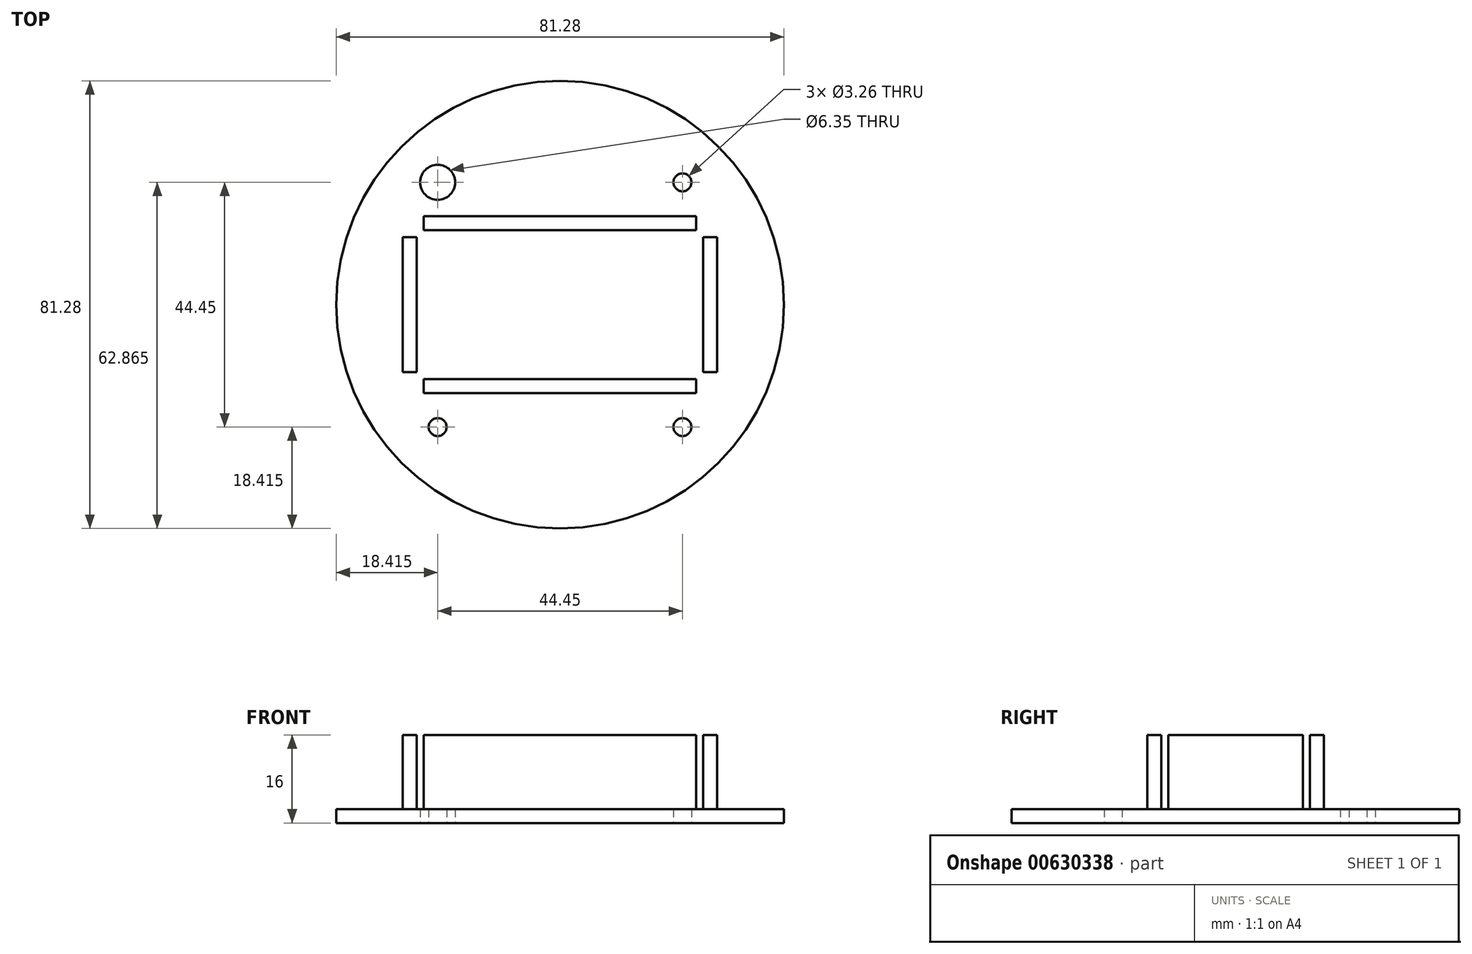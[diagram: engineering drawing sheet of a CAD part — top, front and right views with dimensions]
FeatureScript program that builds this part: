
annotation { "Feature Type Name" : "Feature", "Feature Type Description" : "" }
export const myFeature = defineFeature(function(context is Context, id is Id, definition is map)
    precondition{}
    {
        {
            var Q0;
            Q0=qCreatedBy(makeId("Top.planeOp"),FACE);
            var sketch = newSketch(context, id + "F0", { "sketchPlane" : qUnion([Q0])});
            skLineSegment(sketch, "E0.bottom", {"start": v(-25.4, 25.4) * mm, "end": v(25.4, 25.4) * mm});
            skLineSegment(sketch, "E0.top", {"start": v(-25.4, -25.4) * mm, "end": v(25.4, -25.4) * mm});
            skLineSegment(sketch, "E0.left", {"start": v(-25.4, 25.4) * mm, "end": v(-25.4, -25.4) * mm});
            skLineSegment(sketch, "E0.right", {"start": v(25.4, 25.4) * mm, "end": v(25.4, -25.4) * mm});
            skPoint(sketch, "E0.middle", {"position": v(0, 0) * mm});
            skCircle(sketch, "E1", {"center": v(-22.23, -22.23) * mm, "radius": 1.63 * mm});
            skCircle(sketch, "E2", {"center": v(22.22, 22.23) * mm, "radius": 1.63 * mm});
            skCircle(sketch, "E3", {"center": v(0, 0) * mm, "radius": 38.1 * mm});
            skCircle(sketch, "E4", {"center": v(0, 0) * mm, "radius": 40.64 * mm});
            skLineSegment(sketch, "E5", {"start": v(-25.4, -25.4) * mm, "end": v(25.4, 25.4) * mm});
            skLineSegment(sketch, "E6", {"start": v(-25.4, 25.4) * mm, "end": v(25.4, -25.4) * mm});
            skCircle(sketch, "E7", {"center": v(-22.23, -22.23) * mm, "radius": 3.18 * mm});
            skLineSegment(sketch, "E8", {"start": v(-22.6, -18.12) * mm, "end": v(-33.07, -28.58) * mm});
            skLineSegment(sketch, "E9", {"start": v(-17.1, -21.6) * mm, "end": v(-27.95, -32.44) * mm});
            skCircle(sketch, "E10", {"center": v(22.22, 22.23) * mm, "radius": 3.18 * mm});
            skLineSegment(sketch, "E11", {"start": v(27.08, 31.57) * mm, "end": v(15.84, 20.33) * mm});
            skLineSegment(sketch, "E12", {"start": v(21.85, 17.36) * mm, "end": v(33.43, 28.94) * mm});
            skCircle(sketch, "E13", {"center": v(-22.23, 22.23) * mm, "radius": 1.63 * mm});
            skCircle(sketch, "E14", {"center": v(22.23, -22.23) * mm, "radius": 1.63 * mm});
            skCircle(sketch, "E15", {"center": v(-22.23, 22.23) * mm, "radius": 3.18 * mm});
            skLineSegment(sketch, "E16", {"start": v(-24.44, 19.95) * mm, "end": v(-31.62, 27.13) * mm});
            skLineSegment(sketch, "E17", {"start": v(-19.9, 24.4) * mm, "end": v(-27.14, 31.63) * mm});
            skCircle(sketch, "E18", {"center": v(22.23, -22.23) * mm, "radius": 3.18 * mm});
            skLineSegment(sketch, "E19", {"start": v(19.8, -24.28) * mm, "end": v(28.43, -32.92) * mm});
            skLineSegment(sketch, "E20", {"start": v(23.82, -19.33) * mm, "end": v(35.07, -30.58) * mm});
            skSolve(sketch);
        }
        {
            var Q0;
            {var subQ0=sQuery(id+"F0.wireOp",EDGE,"E16");var subQ1=sQuery(id+"F0.wireOp",EDGE,"E3");var subQ2=makeQuery(id+"F0.imprint","INTERSECT",VERTEX,{"derivedFrom":[subQ1,subQ0]});Q0=makeQuery(id+"F0.imprint","IMPRINT",FACE,{"disambiguationData":[TD([[makeQuery(id+"F0.imprint","IMPRINT",EDGE,{"disambiguationData":[TD([[subQ2,-1.0]])],"derivedFrom":subQ1}),-1.0]])]});}
            var Q1;
            {var subQ0=sQuery(id+"F0.wireOp",EDGE,"E17");var subQ1=sQuery(id+"F0.wireOp",EDGE,"E3");var subQ2=makeQuery(id+"F0.imprint","INTERSECT",VERTEX,{"derivedFrom":[subQ1,subQ0]});Q1=makeQuery(id+"F0.imprint","IMPRINT",FACE,{"disambiguationData":[TD([[makeQuery(id+"F0.imprint","IMPRINT",EDGE,{"disambiguationData":[TD([[subQ2,-1.0]])],"derivedFrom":subQ1}),-1.0]])]});}
            var Q2;
            {var subQ0=sQuery(id+"F0.wireOp",EDGE,"E11");var subQ1=sQuery(id+"F0.wireOp",EDGE,"E3");var subQ2=makeQuery(id+"F0.imprint","INTERSECT",VERTEX,{"derivedFrom":[subQ1,subQ0]});Q2=makeQuery(id+"F0.imprint","IMPRINT",FACE,{"disambiguationData":[TD([[makeQuery(id+"F0.imprint","IMPRINT",EDGE,{"disambiguationData":[TD([[subQ2,-1.0]])],"derivedFrom":subQ1}),-1.0]])]});}
            var Q3;
            {var subQ0=sQuery(id+"F0.wireOp",EDGE,"E11");var subQ1=sQuery(id+"F0.wireOp",EDGE,"E3");var subQ2=makeQuery(id+"F0.imprint","INTERSECT",VERTEX,{"derivedFrom":[subQ1,subQ0]});Q3=makeQuery(id+"F0.imprint","IMPRINT",FACE,{"disambiguationData":[TD([[makeQuery(id+"F0.imprint","IMPRINT",EDGE,{"disambiguationData":[TD([[subQ2,1.0]])],"derivedFrom":subQ1}),-1.0]])]});}
            var Q4;
            {var subQ0=sQuery(id+"F0.wireOp",EDGE,"E12");var subQ1=sQuery(id+"F0.wireOp",EDGE,"E3");var subQ2=makeQuery(id+"F0.imprint","INTERSECT",VERTEX,{"derivedFrom":[subQ1,subQ0]});Q4=makeQuery(id+"F0.imprint","IMPRINT",FACE,{"disambiguationData":[TD([[makeQuery(id+"F0.imprint","IMPRINT",EDGE,{"disambiguationData":[TD([[subQ2,1.0]])],"derivedFrom":subQ1}),-1.0]])]});}
            var Q5;
            {var subQ0=sQuery(id+"F0.wireOp",EDGE,"E19");var subQ1=sQuery(id+"F0.wireOp",EDGE,"E3");var subQ2=makeQuery(id+"F0.imprint","INTERSECT",VERTEX,{"derivedFrom":[subQ1,subQ0]});Q5=makeQuery(id+"F0.imprint","IMPRINT",FACE,{"disambiguationData":[TD([[makeQuery(id+"F0.imprint","IMPRINT",EDGE,{"disambiguationData":[TD([[subQ2,-1.0]])],"derivedFrom":subQ1}),-1.0]])]});}
            var Q6;
            {var subQ0=sQuery(id+"F0.wireOp",EDGE,"E8");var subQ1=sQuery(id+"F0.wireOp",EDGE,"E3");var subQ2=makeQuery(id+"F0.imprint","INTERSECT",VERTEX,{"derivedFrom":[subQ1,subQ0]});Q6=makeQuery(id+"F0.imprint","IMPRINT",FACE,{"disambiguationData":[TD([[makeQuery(id+"F0.imprint","IMPRINT",EDGE,{"disambiguationData":[TD([[subQ2,-1.0]])],"derivedFrom":subQ1}),-1.0]])]});}
            var Q7;
            {var subQ0=sQuery(id+"F0.wireOp",EDGE,"E16");var subQ1=sQuery(id+"F0.wireOp",EDGE,"E0.left");var subQ2=makeQuery(id+"F0.imprint","INTERSECT",VERTEX,{"derivedFrom":[subQ1,subQ0]});Q7=makeQuery(id+"F0.imprint","IMPRINT",FACE,{"disambiguationData":[TD([[makeQuery(id+"F0.imprint","IMPRINT",EDGE,{"disambiguationData":[TD([[subQ2,-1.0]])],"derivedFrom":subQ1}),-1.0]])]});}
            var Q8;
            {var subQ7=sQuery(id+"F0.wireOp",EDGE,"E0.bottom");var subQ10=sQuery(id+"F0.wireOp",EDGE,"E11");var subQ11=makeQuery(id+"F0.imprint","INTERSECT",VERTEX,{"derivedFrom":[subQ7,subQ10]});Q8=makeQuery(id+"F0.imprint","IMPRINT",FACE,{"disambiguationData":[TD([[makeQuery(id+"F0.imprint","IMPRINT",EDGE,{"disambiguationData":[TD([[subQ11,-1.0]])],"derivedFrom":subQ7}),1.0]])]});}
            var Q9;
            {var subQ1=sQuery(id+"F0.wireOp",EDGE,"E0.top");var subQ5=sQuery(id+"F0.wireOp",EDGE,"E19");var subQ6=makeQuery(id+"F0.imprint","INTERSECT",VERTEX,{"derivedFrom":[subQ1,subQ5]});Q9=makeQuery(id+"F0.imprint","IMPRINT",FACE,{"disambiguationData":[TD([[makeQuery(id+"F0.imprint","IMPRINT",EDGE,{"disambiguationData":[TD([[subQ6,-1.0]])],"derivedFrom":subQ1}),-1.0]])]});}
            var Q10;
            {var subQ1=sQuery(id+"F0.wireOp",EDGE,"E0.top");var subQ3=sQuery(id+"F0.wireOp",EDGE,"E7");var subQ7=makeQuery(id+"F0.imprint","INTERSECT",VERTEX,{"derivedFrom":[subQ1,subQ3]});Q10=makeQuery(id+"F0.imprint","IMPRINT",FACE,{"disambiguationData":[TD([[makeQuery(id+"F0.imprint","IMPRINT",EDGE,{"disambiguationData":[TD([[subQ7,-1.0]])],"derivedFrom":subQ1}),-1.0]])]});}
            var Q11;
            {var subQ0=sQuery(id+"F0.wireOp",EDGE,"E9");var subQ1=sQuery(id+"F0.wireOp",EDGE,"E0.top");var subQ2=makeQuery(id+"F0.imprint","INTERSECT",VERTEX,{"derivedFrom":[subQ1,subQ0]});Q11=makeQuery(id+"F0.imprint","IMPRINT",FACE,{"disambiguationData":[TD([[makeQuery(id+"F0.imprint","IMPRINT",EDGE,{"disambiguationData":[TD([[subQ2,-1.0]])],"derivedFrom":subQ1}),-1.0]])]});}
            var Q12;
            {var subQ0=sQuery(id+"F0.wireOp",EDGE,"E9");var subQ1=sQuery(id+"F0.wireOp",EDGE,"E3");var subQ2=makeQuery(id+"F0.imprint","INTERSECT",VERTEX,{"derivedFrom":[subQ1,subQ0]});Q12=makeQuery(id+"F0.imprint","IMPRINT",FACE,{"disambiguationData":[TD([[makeQuery(id+"F0.imprint","IMPRINT",EDGE,{"disambiguationData":[TD([[subQ2,-1.0]])],"derivedFrom":subQ1}),-1.0]])]});}
            var Q13;
            {var subQ1=sQuery(id+"F0.wireOp",EDGE,"E0.left");var subQ3=sQuery(id+"F0.wireOp",EDGE,"E7");var subQ4=makeQuery(id+"F0.imprint","INTERSECT",VERTEX,{"derivedFrom":[subQ1,subQ3]});Q13=makeQuery(id+"F0.imprint","IMPRINT",FACE,{"disambiguationData":[TD([[makeQuery(id+"F0.imprint","IMPRINT",EDGE,{"disambiguationData":[TD([[subQ4,-1.0]])],"derivedFrom":subQ3}),-1.0]])]});}
            var Q14;
            {var subQ1=sQuery(id+"F0.wireOp",EDGE,"E0.top");var subQ3=sQuery(id+"F0.wireOp",EDGE,"E7");var subQ4=makeQuery(id+"F0.imprint","INTERSECT",VERTEX,{"derivedFrom":[subQ1,subQ3]});Q14=makeQuery(id+"F0.imprint","IMPRINT",FACE,{"disambiguationData":[TD([[makeQuery(id+"F0.imprint","IMPRINT",EDGE,{"disambiguationData":[TD([[subQ4,1.0]])],"derivedFrom":subQ3}),-1.0]])]});}
            var Q15;
            {var subQ0=sQuery(id+"F0.wireOp",EDGE,"E5");var subQ1=sQuery(id+"F0.wireOp",EDGE,"E1");var subQ5=makeQuery(id+"F0.imprint","INTERSECT",VERTEX,{"disambiguationData":[OD(0.0)],"derivedFrom":[subQ1,subQ0]});Q15=makeQuery(id+"F0.imprint","IMPRINT",FACE,{"disambiguationData":[TD([[makeQuery(id+"F0.imprint","IMPRINT",EDGE,{"disambiguationData":[TD([[subQ5,1.0]])],"derivedFrom":subQ1}),-1.0]])]});}
            var Q16;
            {var subQ2=sQuery(id+"F0.wireOp",EDGE,"E5");var subQ4=sQuery(id+"F0.wireOp",EDGE,"E1");var subQ5=makeQuery(id+"F0.imprint","INTERSECT",VERTEX,{"disambiguationData":[OD(0.0)],"derivedFrom":[subQ4,subQ2]});Q16=makeQuery(id+"F0.imprint","IMPRINT",FACE,{"disambiguationData":[TD([[makeQuery(id+"F0.imprint","IMPRINT",EDGE,{"disambiguationData":[TD([[subQ5,-1.0]])],"derivedFrom":subQ4}),-1.0]])]});}
            var Q17;
            {var subQ0=sQuery(id+"F0.wireOp",EDGE,"E8");var subQ1=sQuery(id+"F0.wireOp",EDGE,"E0.left");var subQ2=makeQuery(id+"F0.imprint","INTERSECT",VERTEX,{"derivedFrom":[subQ1,subQ0]});Q17=makeQuery(id+"F0.imprint","IMPRINT",FACE,{"disambiguationData":[TD([[makeQuery(id+"F0.imprint","IMPRINT",EDGE,{"disambiguationData":[TD([[subQ2,-1.0]])],"derivedFrom":subQ1}),1.0]])]});}
            var Q18;
            {var subQ0=sQuery(id+"F0.wireOp",EDGE,"E7");var subQ1=sQuery(id+"F0.wireOp",EDGE,"E0.top");var subQ2=makeQuery(id+"F0.imprint","INTERSECT",VERTEX,{"derivedFrom":[subQ1,subQ0]});Q18=makeQuery(id+"F0.imprint","IMPRINT",FACE,{"disambiguationData":[TD([[makeQuery(id+"F0.imprint","IMPRINT",EDGE,{"disambiguationData":[TD([[subQ2,-1.0]])],"derivedFrom":subQ1}),1.0]])]});}
            var Q19;
            {var subQ9=sQuery(id+"F0.wireOp",EDGE,"E0.left");var subQ11=sQuery(id+"F0.wireOp",EDGE,"E16");var subQ12=makeQuery(id+"F0.imprint","INTERSECT",VERTEX,{"derivedFrom":[subQ9,subQ11]});Q19=makeQuery(id+"F0.imprint","IMPRINT",FACE,{"disambiguationData":[TD([[makeQuery(id+"F0.imprint","IMPRINT",EDGE,{"disambiguationData":[TD([[subQ12,-1.0]])],"derivedFrom":subQ9}),1.0]])]});}
            var Q20;
            {var subQ1=sQuery(id+"F0.wireOp",EDGE,"E0.left");var subQ3=sQuery(id+"F0.wireOp",EDGE,"E15");var subQ4=makeQuery(id+"F0.imprint","INTERSECT",VERTEX,{"derivedFrom":[subQ1,subQ3]});Q20=makeQuery(id+"F0.imprint","IMPRINT",FACE,{"disambiguationData":[TD([[makeQuery(id+"F0.imprint","IMPRINT",EDGE,{"disambiguationData":[TD([[subQ4,1.0]])],"derivedFrom":subQ3}),-1.0]])]});}
            var Q21;
            {var subQ0=sQuery(id+"F0.wireOp",EDGE,"E15");var subQ1=sQuery(id+"F0.wireOp",EDGE,"E0.left");var subQ2=makeQuery(id+"F0.imprint","INTERSECT",VERTEX,{"derivedFrom":[subQ1,subQ0]});Q21=makeQuery(id+"F0.imprint","IMPRINT",FACE,{"disambiguationData":[TD([[makeQuery(id+"F0.imprint","IMPRINT",EDGE,{"disambiguationData":[TD([[subQ2,-1.0]])],"derivedFrom":subQ1}),1.0]])]});}
            var Q22;
            {var subQ0=sQuery(id+"F0.wireOp",EDGE,"E15");var subQ1=sQuery(id+"F0.wireOp",EDGE,"E0.bottom");var subQ2=makeQuery(id+"F0.imprint","INTERSECT",VERTEX,{"derivedFrom":[subQ1,subQ0]});Q22=makeQuery(id+"F0.imprint","IMPRINT",FACE,{"disambiguationData":[TD([[makeQuery(id+"F0.imprint","IMPRINT",EDGE,{"disambiguationData":[TD([[subQ2,-1.0]])],"derivedFrom":subQ1}),-1.0]])]});}
            var Q23;
            {var subQ1=sQuery(id+"F0.wireOp",EDGE,"E0.bottom");var subQ3=sQuery(id+"F0.wireOp",EDGE,"E15");var subQ4=makeQuery(id+"F0.imprint","INTERSECT",VERTEX,{"derivedFrom":[subQ1,subQ3]});Q23=makeQuery(id+"F0.imprint","IMPRINT",FACE,{"disambiguationData":[TD([[makeQuery(id+"F0.imprint","IMPRINT",EDGE,{"disambiguationData":[TD([[subQ4,-1.0]])],"derivedFrom":subQ3}),-1.0]])]});}
            var Q24;
            {var subQ0=sQuery(id+"F0.wireOp",EDGE,"E15");var subQ5=sQuery(id+"F0.wireOp",EDGE,"E0.bottom");var subQ7=makeQuery(id+"F0.imprint","INTERSECT",VERTEX,{"derivedFrom":[subQ5,subQ0]});Q24=makeQuery(id+"F0.imprint","IMPRINT",FACE,{"disambiguationData":[TD([[makeQuery(id+"F0.imprint","IMPRINT",EDGE,{"disambiguationData":[TD([[subQ7,-1.0]])],"derivedFrom":subQ5}),1.0]])]});}
            var Q25;
            {var subQ0=sQuery(id+"F0.wireOp",EDGE,"E17");var subQ1=sQuery(id+"F0.wireOp",EDGE,"E0.bottom");var subQ2=makeQuery(id+"F0.imprint","INTERSECT",VERTEX,{"derivedFrom":[subQ1,subQ0]});Q25=makeQuery(id+"F0.imprint","IMPRINT",FACE,{"disambiguationData":[TD([[makeQuery(id+"F0.imprint","IMPRINT",EDGE,{"disambiguationData":[TD([[subQ2,-1.0]])],"derivedFrom":subQ1}),1.0]])]});}
            var Q26;
            {var subQ1=sQuery(id+"F0.wireOp",EDGE,"E0.bottom");var subQ3=sQuery(id+"F0.wireOp",EDGE,"E10");var subQ4=makeQuery(id+"F0.imprint","INTERSECT",VERTEX,{"derivedFrom":[subQ1,subQ3]});Q26=makeQuery(id+"F0.imprint","IMPRINT",FACE,{"disambiguationData":[TD([[makeQuery(id+"F0.imprint","IMPRINT",EDGE,{"disambiguationData":[TD([[subQ4,1.0]])],"derivedFrom":subQ3}),-1.0]])]});}
            var Q27;
            {var subQ1=sQuery(id+"F0.wireOp",EDGE,"E0.right");var subQ3=sQuery(id+"F0.wireOp",EDGE,"E10");var subQ4=makeQuery(id+"F0.imprint","INTERSECT",VERTEX,{"derivedFrom":[subQ1,subQ3]});Q27=makeQuery(id+"F0.imprint","IMPRINT",FACE,{"disambiguationData":[TD([[makeQuery(id+"F0.imprint","IMPRINT",EDGE,{"disambiguationData":[TD([[subQ4,-1.0]])],"derivedFrom":subQ3}),-1.0]])]});}
            var Q28;
            {var subQ0=sQuery(id+"F0.wireOp",EDGE,"E11");var subQ1=sQuery(id+"F0.wireOp",EDGE,"E0.bottom");var subQ2=makeQuery(id+"F0.imprint","INTERSECT",VERTEX,{"derivedFrom":[subQ1,subQ0]});Q28=makeQuery(id+"F0.imprint","IMPRINT",FACE,{"disambiguationData":[TD([[makeQuery(id+"F0.imprint","IMPRINT",EDGE,{"disambiguationData":[TD([[subQ2,-1.0]])],"derivedFrom":subQ1}),-1.0]])]});}
            var Q29;
            {var subQ0=sQuery(id+"F0.wireOp",EDGE,"E10");var subQ1=sQuery(id+"F0.wireOp",EDGE,"E0.right");var subQ2=makeQuery(id+"F0.imprint","INTERSECT",VERTEX,{"derivedFrom":[subQ1,subQ0]});Q29=makeQuery(id+"F0.imprint","IMPRINT",FACE,{"disambiguationData":[TD([[makeQuery(id+"F0.imprint","IMPRINT",EDGE,{"disambiguationData":[TD([[subQ2,-1.0]])],"derivedFrom":subQ1}),-1.0]])]});}
            var Q30;
            {var subQ0=sQuery(id+"F0.wireOp",EDGE,"E12");var subQ1=sQuery(id+"F0.wireOp",EDGE,"E0.right");var subQ2=makeQuery(id+"F0.imprint","INTERSECT",VERTEX,{"derivedFrom":[subQ1,subQ0]});Q30=makeQuery(id+"F0.imprint","IMPRINT",FACE,{"disambiguationData":[TD([[makeQuery(id+"F0.imprint","IMPRINT",EDGE,{"disambiguationData":[TD([[subQ2,-1.0]])],"derivedFrom":subQ1}),1.0]])]});}
            var Q31;
            {var subQ0=sQuery(id+"F0.wireOp",EDGE,"E9");var subQ9=sQuery(id+"F0.wireOp",EDGE,"E0.top");var subQ10=makeQuery(id+"F0.imprint","INTERSECT",VERTEX,{"derivedFrom":[subQ9,subQ0]});Q31=makeQuery(id+"F0.imprint","IMPRINT",FACE,{"disambiguationData":[TD([[makeQuery(id+"F0.imprint","IMPRINT",EDGE,{"disambiguationData":[TD([[subQ10,-1.0]])],"derivedFrom":subQ9}),1.0]])]});}
            var Q32;
            {var subQ0=sQuery(id+"F0.wireOp",EDGE,"E12");var subQ8=sQuery(id+"F0.wireOp",EDGE,"E0.right");var subQ13=makeQuery(id+"F0.imprint","INTERSECT",VERTEX,{"derivedFrom":[subQ8,subQ0]});Q32=makeQuery(id+"F0.imprint","IMPRINT",FACE,{"disambiguationData":[TD([[makeQuery(id+"F0.imprint","IMPRINT",EDGE,{"disambiguationData":[TD([[subQ13,-1.0]])],"derivedFrom":subQ8}),-1.0]])]});}
            var Q33;
            {var subQ9=sQuery(id+"F0.wireOp",EDGE,"E17");var subQ11=sQuery(id+"F0.wireOp",EDGE,"E0.bottom");var subQ12=makeQuery(id+"F0.imprint","INTERSECT",VERTEX,{"derivedFrom":[subQ11,subQ9]});Q33=makeQuery(id+"F0.imprint","IMPRINT",FACE,{"disambiguationData":[TD([[makeQuery(id+"F0.imprint","IMPRINT",EDGE,{"disambiguationData":[TD([[subQ12,-1.0]])],"derivedFrom":subQ11}),-1.0]])]});}
            var Q34;
            {var subQ0=sQuery(id+"F0.wireOp",EDGE,"E19");var subQ1=sQuery(id+"F0.wireOp",EDGE,"E0.top");var subQ2=makeQuery(id+"F0.imprint","INTERSECT",VERTEX,{"derivedFrom":[subQ1,subQ0]});Q34=makeQuery(id+"F0.imprint","IMPRINT",FACE,{"disambiguationData":[TD([[makeQuery(id+"F0.imprint","IMPRINT",EDGE,{"disambiguationData":[TD([[subQ2,-1.0]])],"derivedFrom":subQ1}),1.0]])]});}
            var Q35;
            {var subQ1=sQuery(id+"F0.wireOp",EDGE,"E0.top");var subQ3=sQuery(id+"F0.wireOp",EDGE,"E18");var subQ4=makeQuery(id+"F0.imprint","INTERSECT",VERTEX,{"derivedFrom":[subQ1,subQ3]});Q35=makeQuery(id+"F0.imprint","IMPRINT",FACE,{"disambiguationData":[TD([[makeQuery(id+"F0.imprint","IMPRINT",EDGE,{"disambiguationData":[TD([[subQ4,-1.0]])],"derivedFrom":subQ3}),-1.0]])]});}
            var Q36;
            {var subQ1=sQuery(id+"F0.wireOp",EDGE,"E0.right");var subQ3=sQuery(id+"F0.wireOp",EDGE,"E18");var subQ4=makeQuery(id+"F0.imprint","INTERSECT",VERTEX,{"derivedFrom":[subQ1,subQ3]});Q36=makeQuery(id+"F0.imprint","IMPRINT",FACE,{"disambiguationData":[TD([[makeQuery(id+"F0.imprint","IMPRINT",EDGE,{"disambiguationData":[TD([[subQ4,1.0]])],"derivedFrom":subQ3}),-1.0]])]});}
            var Q37;
            {var subQ0=sQuery(id+"F0.wireOp",EDGE,"E20");var subQ1=sQuery(id+"F0.wireOp",EDGE,"E0.right");var subQ2=makeQuery(id+"F0.imprint","INTERSECT",VERTEX,{"derivedFrom":[subQ1,subQ0]});Q37=makeQuery(id+"F0.imprint","IMPRINT",FACE,{"disambiguationData":[TD([[makeQuery(id+"F0.imprint","IMPRINT",EDGE,{"disambiguationData":[TD([[subQ2,-1.0]])],"derivedFrom":subQ1}),-1.0]])]});}
            var Q38;
            {var subQ0=sQuery(id+"F0.wireOp",EDGE,"E15");var subQ2=sQuery(id+"F0.wireOp",EDGE,"E6");var subQ3=makeQuery(id+"F0.imprint","INTERSECT",VERTEX,{"disambiguationData":[OD(0.0)],"derivedFrom":[subQ2,subQ0]});Q38=makeQuery(id+"F0.imprint","IMPRINT",FACE,{"disambiguationData":[TD([[makeQuery(id+"F0.imprint","IMPRINT",EDGE,{"disambiguationData":[TD([[subQ3,-1.0]])],"derivedFrom":subQ2}),-1.0]])]});}
            var Q39;
            {var subQ1=sQuery(id+"F0.wireOp",EDGE,"E6");var subQ4=sQuery(id+"F0.wireOp",EDGE,"E15");var subQ8=makeQuery(id+"F0.imprint","INTERSECT",VERTEX,{"disambiguationData":[OD(0.0)],"derivedFrom":[subQ1,subQ4]});Q39=makeQuery(id+"F0.imprint","IMPRINT",FACE,{"disambiguationData":[TD([[makeQuery(id+"F0.imprint","IMPRINT",EDGE,{"disambiguationData":[TD([[subQ8,-1.0]])],"derivedFrom":subQ1}),1.0]])]});}
            var Q40;
            {var subQ2=sQuery(id+"F0.wireOp",EDGE,"E5");var subQ4=sQuery(id+"F0.wireOp",EDGE,"E2");var subQ5=makeQuery(id+"F0.imprint","INTERSECT",VERTEX,{"disambiguationData":[OD(0.0)],"derivedFrom":[subQ4,subQ2]});Q40=makeQuery(id+"F0.imprint","IMPRINT",FACE,{"disambiguationData":[TD([[makeQuery(id+"F0.imprint","IMPRINT",EDGE,{"disambiguationData":[TD([[subQ5,-1.0]])],"derivedFrom":subQ4}),-1.0]])]});}
            var Q41;
            {var subQ2=sQuery(id+"F0.wireOp",EDGE,"E5");var subQ4=sQuery(id+"F0.wireOp",EDGE,"E2");var subQ6=makeQuery(id+"F0.imprint","INTERSECT",VERTEX,{"disambiguationData":[OD(0.0)],"derivedFrom":[subQ4,subQ2]});Q41=makeQuery(id+"F0.imprint","IMPRINT",FACE,{"disambiguationData":[TD([[makeQuery(id+"F0.imprint","IMPRINT",EDGE,{"disambiguationData":[TD([[subQ6,1.0]])],"derivedFrom":subQ4}),-1.0]])]});}
            var Q42;
            {var subQ0=sQuery(id+"F0.wireOp",EDGE,"E18");var subQ2=sQuery(id+"F0.wireOp",EDGE,"E6");var subQ3=makeQuery(id+"F0.imprint","INTERSECT",VERTEX,{"disambiguationData":[OD(0.0)],"derivedFrom":[subQ2,subQ0]});Q42=makeQuery(id+"F0.imprint","IMPRINT",FACE,{"disambiguationData":[TD([[makeQuery(id+"F0.imprint","IMPRINT",EDGE,{"disambiguationData":[TD([[subQ3,-1.0]])],"derivedFrom":subQ2}),-1.0]])]});}
            var Q43;
            {var subQ0=sQuery(id+"F0.wireOp",EDGE,"E18");var subQ3=sQuery(id+"F0.wireOp",EDGE,"E6");var subQ4=makeQuery(id+"F0.imprint","INTERSECT",VERTEX,{"disambiguationData":[OD(0.0)],"derivedFrom":[subQ3,subQ0]});Q43=makeQuery(id+"F0.imprint","IMPRINT",FACE,{"disambiguationData":[TD([[makeQuery(id+"F0.imprint","IMPRINT",EDGE,{"disambiguationData":[TD([[subQ4,-1.0]])],"derivedFrom":subQ3}),1.0]])]});}
            extrude(context, id + "F1", {"entities" : qUnion([Q0, Q1, Q2, Q3, Q4, Q5, Q6, Q7, Q8, Q9, Q10, Q11, Q12, Q13, Q14, Q15, Q16, Q17, Q18, Q19, Q20, Q21, Q22, Q23, Q24, Q25, Q26, Q27, Q28, Q29, Q30, Q31, Q32, Q33, Q34, Q35, Q36, Q37, Q38, Q39, Q40, Q41, Q42, Q43]), "depth" : 2.54 * mm, "offsetDistance" : 25.4 * mm});
        }
        {
            var Q0;
            Q0=qCreatedBy(makeId("Top.planeOp"),FACE);
            var sketch = newSketch(context, id + "F2", { "sketchPlane" : qUnion([Q0])});
            skLineSegment(sketch, "E21.bottom", {"start": v(-26, 13.5) * mm, "end": v(26, 13.5) * mm});
            skLineSegment(sketch, "E21.top", {"start": v(-26, -13.5) * mm, "end": v(26, -13.5) * mm});
            skLineSegment(sketch, "E21.left", {"start": v(-26, 13.5) * mm, "end": v(-26, -13.5) * mm});
            skLineSegment(sketch, "E21.right", {"start": v(26, 13.5) * mm, "end": v(26, -13.5) * mm});
            skPoint(sketch, "E21.middle", {"position": v(0, 0) * mm});
            skLineSegment(sketch, "E22.bottom", {"start": v(-28.54, 16.04) * mm, "end": v(28.54, 16.04) * mm});
            skLineSegment(sketch, "E22.top", {"start": v(-28.54, -16.04) * mm, "end": v(28.54, -16.04) * mm});
            skLineSegment(sketch, "E22.left", {"start": v(-28.54, 16.04) * mm, "end": v(-28.54, -16.04) * mm});
            skLineSegment(sketch, "E22.right", {"start": v(28.54, 16.04) * mm, "end": v(28.54, -16.04) * mm});
            skLineSegment(sketch, "E23.bottom", {"start": v(-32.35, 19.85) * mm, "end": v(-24.73, 19.85) * mm});
            skLineSegment(sketch, "E23.top", {"start": v(-32.35, 12.23) * mm, "end": v(-24.73, 12.23) * mm});
            skLineSegment(sketch, "E23.left", {"start": v(-32.35, 19.85) * mm, "end": v(-32.35, 12.23) * mm});
            skLineSegment(sketch, "E23.right", {"start": v(-24.73, 19.85) * mm, "end": v(-24.73, 12.23) * mm});
            skPoint(sketch, "E23.middle", {"position": v(-28.54, 16.04) * mm});
            skLineSegment(sketch, "E24.bottom", {"start": v(24.73, 19.85) * mm, "end": v(32.35, 19.85) * mm});
            skLineSegment(sketch, "E24.top", {"start": v(24.73, 12.23) * mm, "end": v(32.35, 12.23) * mm});
            skLineSegment(sketch, "E24.left", {"start": v(24.73, 19.85) * mm, "end": v(24.73, 12.23) * mm});
            skLineSegment(sketch, "E24.right", {"start": v(32.35, 19.85) * mm, "end": v(32.35, 12.23) * mm});
            skPoint(sketch, "E24.middle", {"position": v(28.54, 16.04) * mm});
            skLineSegment(sketch, "E25.bottom", {"start": v(-32.35, -12.23) * mm, "end": v(-24.73, -12.23) * mm});
            skLineSegment(sketch, "E25.top", {"start": v(-32.35, -19.85) * mm, "end": v(-24.73, -19.85) * mm});
            skLineSegment(sketch, "E25.left", {"start": v(-32.35, -12.23) * mm, "end": v(-32.35, -19.85) * mm});
            skLineSegment(sketch, "E25.right", {"start": v(-24.73, -12.23) * mm, "end": v(-24.73, -19.85) * mm});
            skPoint(sketch, "E25.middle", {"position": v(-28.54, -16.04) * mm});
            skLineSegment(sketch, "E26.bottom", {"start": v(24.73, -12.23) * mm, "end": v(32.35, -12.23) * mm});
            skLineSegment(sketch, "E26.top", {"start": v(24.73, -19.85) * mm, "end": v(32.35, -19.85) * mm});
            skLineSegment(sketch, "E26.left", {"start": v(24.73, -12.23) * mm, "end": v(24.73, -19.85) * mm});
            skLineSegment(sketch, "E26.right", {"start": v(32.35, -12.23) * mm, "end": v(32.35, -19.85) * mm});
            skPoint(sketch, "E26.middle", {"position": v(28.54, -16.04) * mm});
            skSolve(sketch);
        }
        {
            var Q0;
            {var subQ0=sQuery(id+"F2.wireOp",EDGE,"E23.top");var subQ1=sQuery(id+"F2.wireOp",EDGE,"E21.left");var subQ2=makeQuery(id+"F2.imprint","INTERSECT",VERTEX,{"derivedFrom":[subQ1,subQ0]});Q0=makeQuery(id+"F2.imprint","IMPRINT",FACE,{"disambiguationData":[TD([[makeQuery(id+"F2.imprint","IMPRINT",EDGE,{"disambiguationData":[TD([[subQ2,-1.0]])],"derivedFrom":subQ1}),-1.0]])]});}
            var Q1;
            {var subQ0=sQuery(id+"F2.wireOp",EDGE,"E23.right");var subQ1=sQuery(id+"F2.wireOp",EDGE,"E21.bottom");var subQ2=makeQuery(id+"F2.imprint","INTERSECT",VERTEX,{"derivedFrom":[subQ1,subQ0]});Q1=makeQuery(id+"F2.imprint","IMPRINT",FACE,{"disambiguationData":[TD([[makeQuery(id+"F2.imprint","IMPRINT",EDGE,{"disambiguationData":[TD([[subQ2,-1.0]])],"derivedFrom":subQ1}),1.0]])]});}
            var Q2;
            {var subQ0=sQuery(id+"F2.wireOp",EDGE,"E24.top");var subQ1=sQuery(id+"F2.wireOp",EDGE,"E21.right");var subQ2=makeQuery(id+"F2.imprint","INTERSECT",VERTEX,{"derivedFrom":[subQ1,subQ0]});Q2=makeQuery(id+"F2.imprint","IMPRINT",FACE,{"disambiguationData":[TD([[makeQuery(id+"F2.imprint","IMPRINT",EDGE,{"disambiguationData":[TD([[subQ2,-1.0]])],"derivedFrom":subQ1}),1.0]])]});}
            var Q3;
            {var subQ0=sQuery(id+"F2.wireOp",EDGE,"E25.right");var subQ1=sQuery(id+"F2.wireOp",EDGE,"E21.top");var subQ2=makeQuery(id+"F2.imprint","INTERSECT",VERTEX,{"derivedFrom":[subQ1,subQ0]});Q3=makeQuery(id+"F2.imprint","IMPRINT",FACE,{"disambiguationData":[TD([[makeQuery(id+"F2.imprint","IMPRINT",EDGE,{"disambiguationData":[TD([[subQ2,-1.0]])],"derivedFrom":subQ1}),-1.0]])]});}
            extrude(context, id + "F3", {"entities" : qUnion([Q0, Q1, Q2, Q3]), "operationType" : NewBodyOperationType.ADD, "depth" : 16 * mm, "offsetDistance" : 25.4 * mm});
        }
    });
